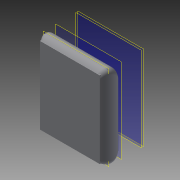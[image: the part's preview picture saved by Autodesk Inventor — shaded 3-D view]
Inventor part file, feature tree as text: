
AUTODESK INVENTOR PART (.ipt)
format: ipt  version: 2014 (Build 180170000, 170)  size: 231,936 bytes
history: native  units: mm
features: plane x4, sketch x3, extrude x1, loft x1, fillet x1, other x1
ambient origin geometry x8: Origin, YZ Plane, XZ Plane, XY Plane, X Axis, Y Axis, Z Axis, Center Point
bodies: Solid1 (feature_tree)
feature tree (11):
  extrude  "Extrusion1"  Depth=90.0mm
  plane  "Work Plane1"
  plane  "Work Plane2"
  plane  "Work Plane3"
  plane  "Work Plane4"
  loft  "Loft1"
  fillet  "Fillet1"  Radius=7.0mm
  sketch  "Sketch1"  dims[d0=70.0mm d1=90.0mm]
  sketch  "Sketch2"  dims[d2=0.4mm d3=0.0mm d4=47.6mm d5=7.0mm]
  sketch  "Sketch4"  dims[d6=45.0mm d7=21.5mm d9=80.0mm d10=0.0mm d11=90.0deg d12=0.0mm d13=90.0deg d14=0.0mm d15=90.0deg d16=5.0mm]
  other  "Edges1"
